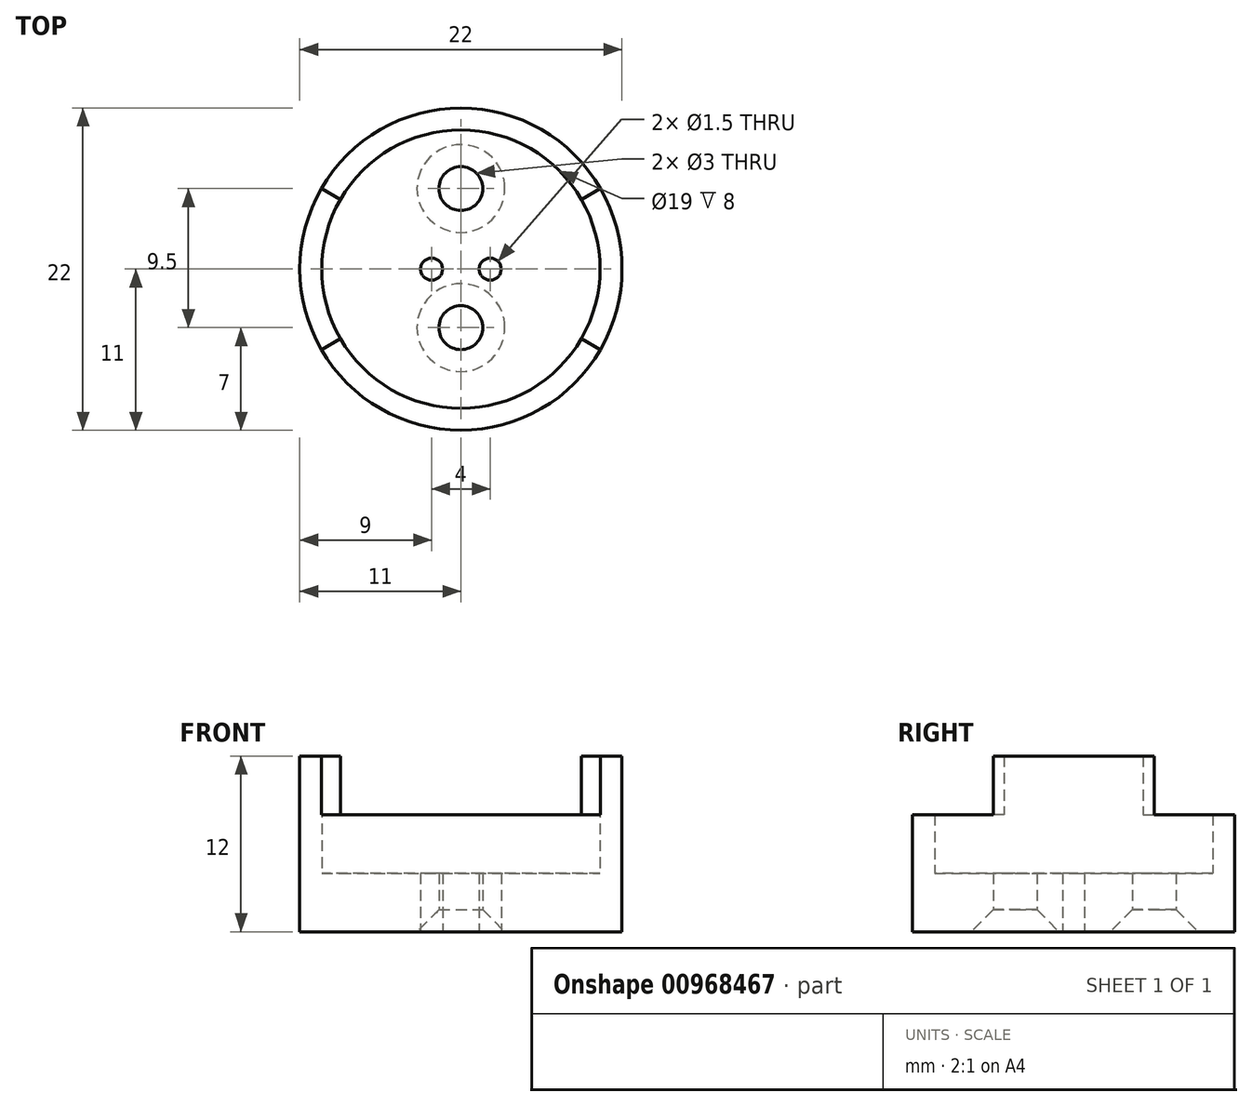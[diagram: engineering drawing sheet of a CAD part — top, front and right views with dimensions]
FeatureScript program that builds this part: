
annotation { "Feature Type Name" : "Feature", "Feature Type Description" : "" }
export const myFeature = defineFeature(function(context is Context, id is Id, definition is map)
    precondition{}
    {
        {
            var Q0;
            Q0=qCreatedBy(makeId("Top.planeOp"),FACE);
            var sketch = newSketch(context, id + "F0", { "sketchPlane" : qUnion([Q0])});
            skCircle(sketch, "E0", {"center": v(0, 0) * mm, "radius": 11 * mm});
            skPoint(sketch, "E1", {"position": v(2, 0) * mm});
            skPoint(sketch, "E2", {"position": v(-2, 0) * mm});
            skCircle(sketch, "E3", {"center": v(0, 0) * mm, "radius": 9.5 * mm});
            skLineSegment(sketch, "E4", {"start": v(-8.23, 4.75) * mm, "end": v(-9.53, 5.5) * mm});
            skLineSegment(sketch, "E5", {"start": v(-12.3, 0) * mm, "end": v(-21.68, 0) * mm});
            skLineSegment(sketch, "E6", {"start": v(0, -12.82) * mm, "end": v(0, -20.2) * mm});
            skLineSegment(sketch, "E7.MirrorCS", {"start": v(-8.23, -4.75) * mm, "end": v(-9.53, -5.5) * mm});
            skLineSegment(sketch, "E8.MirrorCS", {"start": v(8.23, -4.75) * mm, "end": v(9.53, -5.5) * mm});
            skLineSegment(sketch, "E9.MirrorCS", {"start": v(8.23, 4.75) * mm, "end": v(9.53, 5.5) * mm});
            skPoint(sketch, "E10", {"position": v(0, -4) * mm});
            skPoint(sketch, "E11", {"position": v(0, 5.5) * mm});
            skSolve(sketch);
        }
        {
            var Q0;
            {var subQ0=sQuery(id+"F0.wireOp",EDGE,"E4");Q0=makeQuery(id+"F0.imprint","IMPRINT",FACE,{"disambiguationData":[TD([[makeQuery(id+"F0.imprint","IMPRINT",EDGE,{"derivedFrom":subQ0}),-1.0]])]});}
            var Q1;
            {var subQ0=sQuery(id+"F0.wireOp",EDGE,"E7.MirrorCS");Q1=makeQuery(id+"F0.imprint","IMPRINT",FACE,{"disambiguationData":[TD([[makeQuery(id+"F0.imprint","IMPRINT",EDGE,{"derivedFrom":subQ0}),1.0]])]});}
            extrude(context, id + "F1", {"entities" : qUnion([Q0, Q1]), "depth" : 8 * mm, "offsetDistance" : 25 * mm});
        }
        {
            var Q0;
            Q0=makeQuery(id+"F0.imprint","IMPRINT",FACE,{"disambiguationData":[TD([[makeQuery(id+"F0.imprint","IMPRINT",EDGE,{"derivedFrom":sQuery(id+"F0.wireOp",EDGE,"E3")}),1.0]])]});
            extrude(context, id + "F2", {"entities" : qUnion([Q0]), "operationType" : NewBodyOperationType.ADD, "depth" : 4 * mm, "offsetDistance" : 25 * mm});
        }
        {
            var Q0;
            Q0=sQuery(id+"F0.wireOp",VERTEX,"E1");
            var Q1;
            Q1=sQuery(id+"F0.wireOp",VERTEX,"E2");
            var Q2;
            Q2=makeQuery(id+"F1.opExtrude","SWEPT_BODY",BODY,{"disambiguationData":[OSD([sQuery(id+"F0.wireOp",EDGE,"E0"),sQuery(id+"F0.wireOp",EDGE,"E3")])]});
            hole(context, id + "F3", {"style" : HoleStyle.SIMPLE, "endStyle" : HoleEndStyle.THROUGH, "oppositeDirection" : true, "holeDiameter" : 1.5 * mm, "majorDiameter" : 5 * mm, "isTappedThrough" : true, "tappedDepth" : 12 * mm, "tapClearance" : 3, "locations" : qUnion([Q0, Q1]), "scope" : qUnion([Q2])});
        }
        {
            var Q0;
            {var subQ0=sQuery(id+"F0.wireOp",EDGE,"E4");Q0=makeQuery(id+"F0.imprint","IMPRINT",FACE,{"disambiguationData":[TD([[makeQuery(id+"F0.imprint","IMPRINT",EDGE,{"derivedFrom":subQ0}),1.0]])]});}
            var Q1;
            {var subQ0=sQuery(id+"F0.wireOp",EDGE,"E8.MirrorCS");Q1=makeQuery(id+"F0.imprint","IMPRINT",FACE,{"disambiguationData":[TD([[makeQuery(id+"F0.imprint","IMPRINT",EDGE,{"derivedFrom":subQ0}),1.0]])]});}
            extrude(context, id + "F4", {"entities" : qUnion([Q0, Q1]), "operationType" : NewBodyOperationType.ADD, "depth" : 12 * mm, "offsetDistance" : 25 * mm});
        }
        {
            var Q0;
            Q0=sQuery(id+"F0.wireOp",VERTEX,"E10");
            var Q1;
            Q1=sQuery(id+"F0.wireOp",VERTEX,"E11");
            var Q2;
            Q2=makeQuery(id+"F1.opExtrude","SWEPT_BODY",BODY,{"disambiguationData":[OSD([sQuery(id+"F0.wireOp",EDGE,"E0"),sQuery(id+"F0.wireOp",EDGE,"E3"),sQuery(id+"F0.wireOp",EDGE,"E4"),sQuery(id+"F0.wireOp",EDGE,"E9.MirrorCS")])]});
            hole(context, id + "F5", {"style" : HoleStyle.C_SINK, "endStyle" : HoleEndStyle.THROUGH, "oppositeDirection" : true, "holeDiameter" : 3 * mm, "cSinkDiameter" : 6 * mm, "cSinkAngle" : 90 * degree, "majorDiameter" : 5 * mm, "isTappedThrough" : true, "tappedDepth" : 12 * mm, "tapClearance" : 3, "locations" : qUnion([Q0, Q1]), "scope" : qUnion([Q2])});
        }
    });
